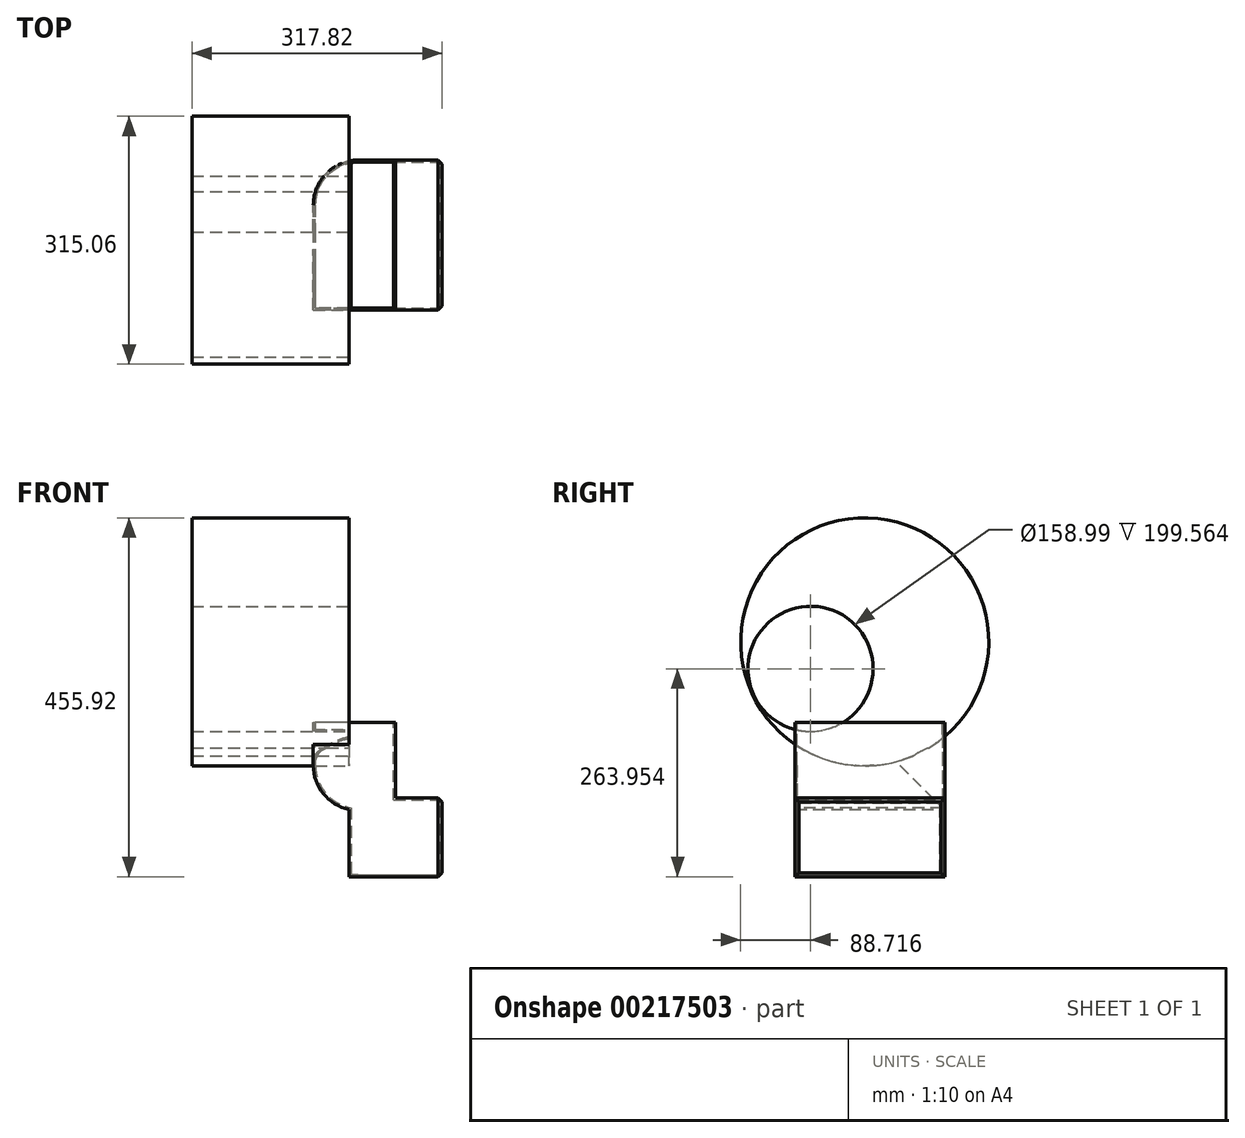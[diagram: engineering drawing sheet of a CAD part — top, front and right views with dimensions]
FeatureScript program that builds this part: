
annotation { "Feature Type Name" : "Feature", "Feature Type Description" : "" }
export const myFeature = defineFeature(function(context is Context, id is Id, definition is map)
    precondition{}
    {
        {
            var Q0;
            Q0=qCreatedBy(makeId("Front.planeOp"),FACE);
            var sketch = newSketch(context, id + "F0", { "sketchPlane" : qUnion([Q0])});
            skLineSegment(sketch, "E0.bottom", {"start": v(59.13, -14.41) * mm, "end": v(-45.45, -14.41) * mm});
            skLineSegment(sketch, "E0.top", {"start": v(59.13, 96.08) * mm, "end": v(-45.45, 96.08) * mm});
            skLineSegment(sketch, "E0.left", {"start": v(59.13, -14.41) * mm, "end": v(59.13, 96.08) * mm});
            skLineSegment(sketch, "E0.right", {"start": v(-45.45, -14.41) * mm, "end": v(-45.45, 96.08) * mm});
            skLineSegment(sketch, "E1.bottom", {"start": v(0, 0) * mm, "end": v(118.26, 0) * mm});
            skLineSegment(sketch, "E1.top", {"start": v(0, -99.78) * mm, "end": v(118.26, -99.78) * mm});
            skLineSegment(sketch, "E1.left", {"start": v(0, 0) * mm, "end": v(0, -99.78) * mm});
            skLineSegment(sketch, "E1.right", {"start": v(118.26, 0) * mm, "end": v(118.26, -99.78) * mm});
            skSolve(sketch);
        }
        {
            var Q0;
            Q0 = qSketchRegion(id + "F0", true);
            extrude(context, id + "F1", {"entities" : qUnion([Q0]), "depth" : 25.4 * mm});
        }
        {
            var Q0;
            Q0=makeQuery(id+"F1.opExtrude","CAP_FACE",FACE,{"disambiguationData":[OSD([sQuery(id+"F0.wireOp",EDGE,"E0.bottom"),sQuery(id+"F0.wireOp",EDGE,"E0.top"),sQuery(id+"F0.wireOp",EDGE,"E0.left"),sQuery(id+"F0.wireOp",EDGE,"E0.right"),sQuery(id+"F0.wireOp",EDGE,"E1.bottom"),sQuery(id+"F0.wireOp",EDGE,"E1.top"),sQuery(id+"F0.wireOp",EDGE,"E1.left"),sQuery(id+"F0.wireOp",EDGE,"E1.right")])],"isStart":false});
            extrude(context, id + "F2", {"entities" : qUnion([Q0]), "operationType" : NewBodyOperationType.ADD, "depth" : 165.03 * mm});
        }
        {
            var Q0;
            {var subQ0=sQuery(id+"F0.wireOp",EDGE,"E1.right");var subQ1=sQuery(id+"F0.wireOp",EDGE,"E1.bottom");Q0=makeQuery(id+"F2.boolean.opBoolean","MERGE",EDGE,{"derivedFrom":[makeQuery(id+"F1.opExtrude","SWEPT_EDGE",EDGE,{"disambiguationData":[OSD([subQ1,subQ0])]}),makeQuery(id+"F2.opExtrude","SWEPT_EDGE",EDGE,{"disambiguationData":[OSD([subQ1,subQ0])]})]});}
            var Q1;
            Q1=makeQuery(id+"F1.opExtrude","CAP_EDGE",EDGE,{"disambiguationData":[OSD([sQuery(id+"F0.wireOp",EDGE,"E1.right")])],"isStart":true});
            var Q2;
            {var subQ0=sQuery(id+"F0.wireOp",EDGE,"E1.right");var subQ1=sQuery(id+"F0.wireOp",EDGE,"E1.top");Q2=makeQuery(id+"F2.boolean.opBoolean","MERGE",EDGE,{"derivedFrom":[makeQuery(id+"F1.opExtrude","SWEPT_EDGE",EDGE,{"disambiguationData":[OSD([subQ1,subQ0])]}),makeQuery(id+"F2.opExtrude","SWEPT_EDGE",EDGE,{"disambiguationData":[OSD([subQ1,subQ0])]})]});}
            var Q3;
            Q3=makeQuery(id+"F2.opExtrude","CAP_EDGE",EDGE,{"disambiguationData":[OSD([sQuery(id+"F0.wireOp",EDGE,"E1.right")])],"isStart":false});
            chamfer(context, id + "F3", {"entities" : qUnion([Q0, Q1, Q2, Q3]), "width" : 5.08 * mm, "tangentPropagation" : true});
        }
        {
            var Q0;
            {var subQ0=sQuery(id+"F0.wireOp",EDGE,"E0.right");var subQ1=sQuery(id+"F0.wireOp",EDGE,"E0.bottom");Q0=makeQuery(id+"F2.boolean.opBoolean","MERGE",EDGE,{"derivedFrom":[makeQuery(id+"F1.opExtrude","SWEPT_EDGE",EDGE,{"disambiguationData":[OSD([subQ1,subQ0])]}),makeQuery(id+"F2.opExtrude","SWEPT_EDGE",EDGE,{"disambiguationData":[OSD([subQ1,subQ0])]})]});}
            var Q1;
            Q1=makeQuery(id+"F1.opExtrude","CAP_EDGE",EDGE,{"disambiguationData":[OSD([sQuery(id+"F0.wireOp",EDGE,"E0.right")])],"isStart":true});
            fillet(context, id + "F4", {"entities" : qUnion([Q0, Q1]), "radius" : 57.15 * mm, "tangentPropagation" : true, "allowEdgeOverflow" : false});
        }
        {
            var Q0;
            {var subQ0=sQuery(id+"F0.wireOp",EDGE,"E0.top");Q0=makeQuery(id+"F2.boolean.opBoolean","MERGE",FACE,{"derivedFrom":[makeQuery(id+"F1.opExtrude","SWEPT_FACE",FACE,{"disambiguationData":[OSD([subQ0])]}),makeQuery(id+"F2.opExtrude","SWEPT_FACE",FACE,{"disambiguationData":[OSD([subQ0])]})]});}
            shell(context, id + "F5", {"entities" : qUnion([Q0]), "thickness" : 2.54 * mm});
        }
        {
            var Q0;
            Q0=qCreatedBy(makeId("Right.planeOp"),FACE);
            var sketch = newSketch(context, id + "F6", { "sketchPlane" : qUnion([Q0])});
            skCircle(sketch, "E2", {"center": v(0, 0) * mm, "radius": 67 * mm});
            skSolve(sketch);
        }
        {
            var Q0;
            Q0=makeQuery(id+"F6.imprint","IMPRINT",FACE,{"disambiguationData":[TD([[makeQuery(id+"F6.imprint","IMPRINT",EDGE,{"derivedFrom":sQuery(id+"F6.wireOp",EDGE,"E2")}),1.0]])]});
            var sketch = newSketch(context, id + "F7", { "sketchPlane" : qUnion([Q0])});
            skCircle(sketch, "E3", {"center": v(-101.9, 198.6) * mm, "radius": 157.53 * mm});
            skCircle(sketch, "E4", {"center": v(-170.71, 164.17) * mm, "radius": 79.5 * mm});
            skSolve(sketch);
        }
        {
            var Q0;
            Q0=makeQuery(id+"F7.imprint","IMPRINT",FACE,{"disambiguationData":[TD([[makeQuery(id+"F7.imprint","IMPRINT",EDGE,{"derivedFrom":sQuery(id+"F7.wireOp",EDGE,"E4")}),-1.0]])]});
            extrude(context, id + "F8", {"entities" : qUnion([Q0]), "operationType" : NewBodyOperationType.ADD, "oppositeDirection" : true, "depth" : 199.56 * mm});
        }
    });
